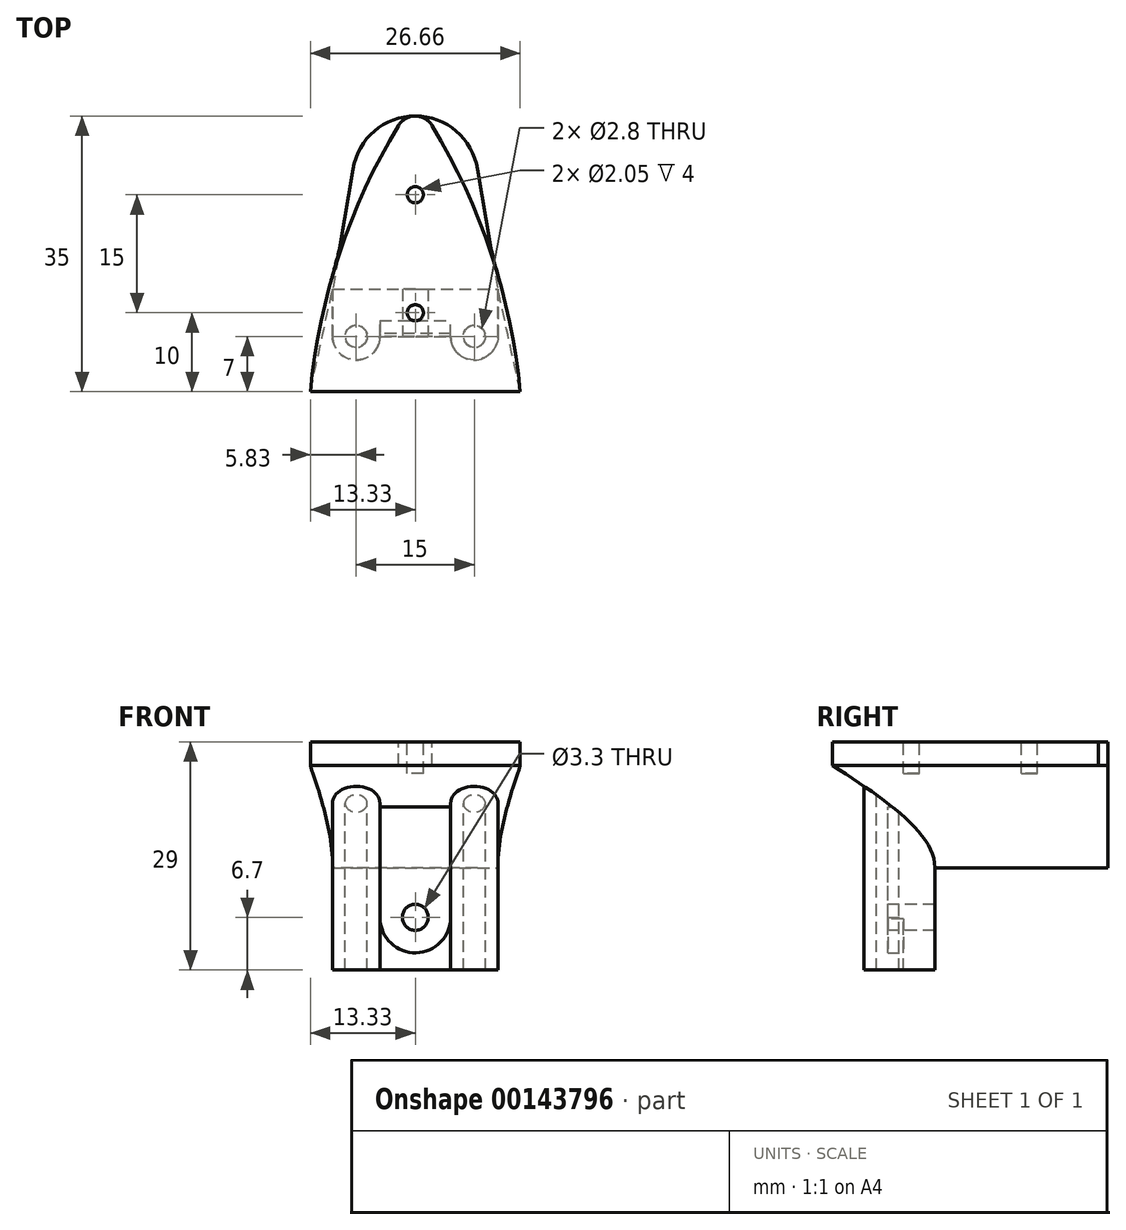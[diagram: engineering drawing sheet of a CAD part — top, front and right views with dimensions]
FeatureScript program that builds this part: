
annotation { "Feature Type Name" : "Feature", "Feature Type Description" : "" }
export const myFeature = defineFeature(function(context is Context, id is Id, definition is map)
    precondition{}
    {
        {
            var Q0;
            Q0=qCreatedBy(makeId("Top.planeOp"),FACE);
            var sketch = newSketch(context, id + "F0", { "sketchPlane" : qUnion([Q0])});
            skPoint(sketch, "E0.0", {"position": v(2.16, 66.26) * mm});
            skArc(sketch, "E1.0", {"start": v(-2.16, 66.26) * mm, "mid": v(0, 67.5) * mm, "end": v(2.16, 66.26) * mm});
            skArc(sketch, "E2.0", {"start": v(-13.33, 32.5) * mm, "mid": v(-9.64, 50.01) * mm, "end": v(-2.16, 66.26) * mm});
            skLineSegment(sketch, "E3.0", {"start": v(-13.33, 32.5) * mm, "end": v(13.33, 32.5) * mm});
            skArc(sketch, "E4.0", {"start": v(13.33, 32.5) * mm, "mid": v(9.64, 50.01) * mm, "end": v(2.16, 66.26) * mm});
            skSolve(sketch);
        }
        {
            var Q0;
            Q0 = qSketchRegion(id + "F0", true);
            extrude(context, id + "F1", {"entities" : qUnion([Q0]), "oppositeDirection" : true, "depth" : 3 * mm, "offsetDistance" : 25 * mm});
        }
        {
            var Q0;
            Q0=qCreatedBy(makeId("Top.planeOp"),FACE);
            cPlane(context, id + "F2", {"entities" : qUnion([Q0]), "cplaneType" : CPlaneType.OFFSET, "offset" : 16 * mm, "oppositeDirection" : true, "width" : 150 * mm, "height" : 150 * mm});
        }
        {
            var Q0;
            Q0=qCreatedBy(id+"F2.planeOp",FACE);
            var sketch = newSketch(context, id + "F3", { "sketchPlane" : qUnion([Q0])});
            skPoint(sketch, "E5.visualSharp", {"position": v(10.5, 45.5) * mm});
            skPoint(sketch, "E6.visualSharp", {"position": v(-10.5, 45.5) * mm});
            skArc(sketch, "E7", {"start": v(7.9, 60.73) * mm, "mid": v(0.01, 67.5) * mm, "end": v(-7.9, 60.75) * mm});
            skLineSegment(sketch, "E8", {"start": v(-7.9, 60.75) * mm, "end": v(-10.5, 45.5) * mm});
            skLineSegment(sketch, "E9", {"start": v(7.9, 60.73) * mm, "end": v(10.5, 45.5) * mm});
            skLineSegment(sketch, "E10", {"start": v(-10.5, 45.5) * mm, "end": v(10.5, 45.5) * mm});
            skSolve(sketch);
        }
        {
            var Q0;
            Q0=makeQuery(id+"F1.opExtrude","CAP_FACE",FACE,{"disambiguationData":[OSD([sQuery(id+"F0.wireOp",EDGE,"E1.0"),sQuery(id+"F0.wireOp",EDGE,"E2.0"),sQuery(id+"F0.wireOp",EDGE,"E3.0"),sQuery(id+"F0.wireOp",EDGE,"E4.0")])],"isStart":false});
            var Q1;
            Q1 = qSketchRegion(id + "F3", true);
            loft(context, id + "F4", {"operationType" : NewBodyOperationType.ADD, "sheetProfilesArray" : [{ "sheetProfileEntities" : qUnion([Q0]) }, { "sheetProfileEntities" : qUnion([Q1]) }], "endCondition" : LoftEndDerivativeType.NORMAL_TO_PROFILE, "endMagnitude" : 1});
        }
        {
            var Q0;
            Q0=qCreatedBy(makeId("Top.planeOp"),FACE);
            var sketch = newSketch(context, id + "F5", { "sketchPlane" : qUnion([Q0])});
            skLineSegment(sketch, "E11.0", {"start": v(10.5, 45.5) * mm, "end": v(-10.5, 45.5) * mm});
            skLineSegment(sketch, "E12", {"start": v(-10.5, 45.5) * mm, "end": v(-10.5, 41.5) * mm});
            skLineSegment(sketch, "E13", {"start": v(-4.5, 41.5) * mm, "end": v(4.5, 41.5) * mm});
            skLineSegment(sketch, "E14", {"start": v(10.5, 41.5) * mm, "end": v(10.5, 45.5) * mm});
            skLineSegment(sketch, "E15", {"start": v(-10.5, 41.5) * mm, "end": v(-10.5, 39.5) * mm});
            skLineSegment(sketch, "E16", {"start": v(-7.5, 36.5) * mm, "end": v(-7.5, 36.5) * mm});
            skLineSegment(sketch, "E17", {"start": v(-4.5, 41.5) * mm, "end": v(-4.5, 39.5) * mm});
            skPoint(sketch, "E18.visualSharp", {"position": v(-10.5, 36.5) * mm});
            skArc(sketch, "E18.filletArc", {"start": v(-10.5, 39.5) * mm, "mid": v(-9.62, 37.38) * mm, "end": v(-7.5, 36.5) * mm});
            skPoint(sketch, "E19.visualSharp", {"position": v(-4.5, 36.5) * mm});
            skArc(sketch, "E19.filletArc", {"start": v(-7.5, 36.5) * mm, "mid": v(-5.38, 37.38) * mm, "end": v(-4.5, 39.5) * mm});
            skCircle(sketch, "E20", {"center": v(-7.5, 39.5) * mm, "radius": 1.4 * mm});
            skArc(sketch, "E21.MirrorCS", {"start": v(7.5, 36.5) * mm, "mid": v(5.38, 37.38) * mm, "end": v(4.5, 39.5) * mm});
            skLineSegment(sketch, "E22.MirrorCS", {"start": v(4.5, 41.5) * mm, "end": v(4.5, 39.5) * mm});
            skCircle(sketch, "E23.MirrorC", {"center": v(7.5, 39.5) * mm, "radius": 1.4 * mm});
            skArc(sketch, "E24.MirrorCS", {"start": v(10.5, 39.5) * mm, "mid": v(9.62, 37.38) * mm, "end": v(7.5, 36.5) * mm});
            skLineSegment(sketch, "E25.MirrorCS", {"start": v(10.5, 41.5) * mm, "end": v(10.5, 39.5) * mm});
            skSolve(sketch);
        }
        {
            var Q0;
            Q0 = qSketchRegion(id + "F5", true);
            extrude(context, id + "F6", {"entities" : qUnion([Q0]), "operationType" : NewBodyOperationType.ADD, "oppositeDirection" : true, "depth" : 29 * mm, "offsetDistance" : 25 * mm});
        }
        {
            var Q0;
            Q0=makeQuery(id+"F6.boolean.opBoolean","INTERSECT",EDGE,{"derivedFrom":[makeQuery(id+"F4.opLoft","SWEPT_FACE",FACE,{"disambiguationData":[OSD([sQuery(id+"F0.wireOp",EDGE,"E2.0"),sQuery(id+"F0.wireOp",EDGE,"E3.0"),sQuery(id+"F0.wireOp",EDGE,"E4.0"),sQuery(id+"F3.wireOp",EDGE,"E8"),sQuery(id+"F3.wireOp",EDGE,"E9"),sQuery(id+"F3.wireOp",EDGE,"E10")])]}),makeQuery(id+"F6.opExtrude","SWEPT_FACE",FACE,{"disambiguationData":[OSD([sQuery(id+"F5.wireOp",EDGE,"E13")])]})]});
            fillet(context, id + "F7", {"entities" : qUnion([Q0]), "tangentPropagation" : true, "radius" : 7 * mm, "defaultsChanged" : true, "vertexSettings" : [], "allowEdgeOverflow" : false});
        }
        {
            var Q0;
            Q0=makeQuery(id+"F6.opExtrude","SWEPT_FACE",FACE,{"disambiguationData":[OSD([sQuery(id+"F5.wireOp",EDGE,"E13")])]});
            var sketch = newSketch(context, id + "F8", { "sketchPlane" : qUnion([Q0])});
            skCircle(sketch, "E26", {"center": v(0, -22.3) * mm, "radius": 1.65 * mm});
            skSolve(sketch);
        }
        {
            var Q0;
            Q0 = qSketchRegion(id + "F8", true);
            extrude(context, id + "F9", {"entities" : qUnion([Q0]), "operationType" : NewBodyOperationType.REMOVE, "oppositeDirection" : true, "depth" : 25 * mm, "offsetDistance" : 25 * mm});
        }
        {
            var Q0;
            Q0=makeQuery(id+"F6.opExtrude","SWEPT_FACE",FACE,{"disambiguationData":[OSD([sQuery(id+"F5.wireOp",EDGE,"E13")])]});
            var sketch = newSketch(context, id + "F10", { "sketchPlane" : qUnion([Q0])});
            skArc(sketch, "E27", {"start": v(-4.5, -22.48) * mm, "mid": v(0.18, -26.8) * mm, "end": v(4.5, -22.12) * mm});
            skLineSegment(sketch, "E28.bottom", {"start": v(-4.5, -22.48) * mm, "end": v(-4.5, -22.48) * mm});
            skLineSegment(sketch, "E28.top", {"start": v(4.5, -8.28) * mm, "end": v(-4.5, -8.28) * mm});
            skLineSegment(sketch, "E28.left", {"start": v(4.5, -22.48) * mm, "end": v(4.5, -8.28) * mm});
            skLineSegment(sketch, "E28.right", {"start": v(-4.5, -22.48) * mm, "end": v(-4.5, -8.28) * mm});
            skCircle(sketch, "E29.0", {"center": v(0, -22.3) * mm, "radius": 1.65 * mm});
            skSolve(sketch);
        }
        {
            var Q0;
            Q0 = qSketchRegion(id + "F10", true);
            extrude(context, id + "F11", {"entities" : qUnion([Q0]), "operationType" : NewBodyOperationType.ADD, "depth" : 2 * mm, "offsetDistance" : 25 * mm});
        }
        {
            var Q0;
            Q0=makeQuery(id+"F1.opExtrude","CAP_FACE",FACE,{"disambiguationData":[OSD([sQuery(id+"F0.wireOp",EDGE,"E1.0"),sQuery(id+"F0.wireOp",EDGE,"E2.0"),sQuery(id+"F0.wireOp",EDGE,"E3.0"),sQuery(id+"F0.wireOp",EDGE,"E4.0")])],"isStart":true});
            var sketch = newSketch(context, id + "F12", { "sketchPlane" : qUnion([Q0])});
            skCircle(sketch, "E30", {"center": v(0, 57.5) * mm, "radius": 1.02 * mm});
            skCircle(sketch, "E31", {"center": v(0, 42.5) * mm, "radius": 1.02 * mm});
            skSolve(sketch);
        }
        {
            var Q0;
            Q0 = qSketchRegion(id + "F12", true);
            extrude(context, id + "F13", {"entities" : qUnion([Q0]), "operationType" : NewBodyOperationType.REMOVE, "oppositeDirection" : true, "depth" : 4 * mm, "offsetDistance" : 25 * mm});
        }
    });
